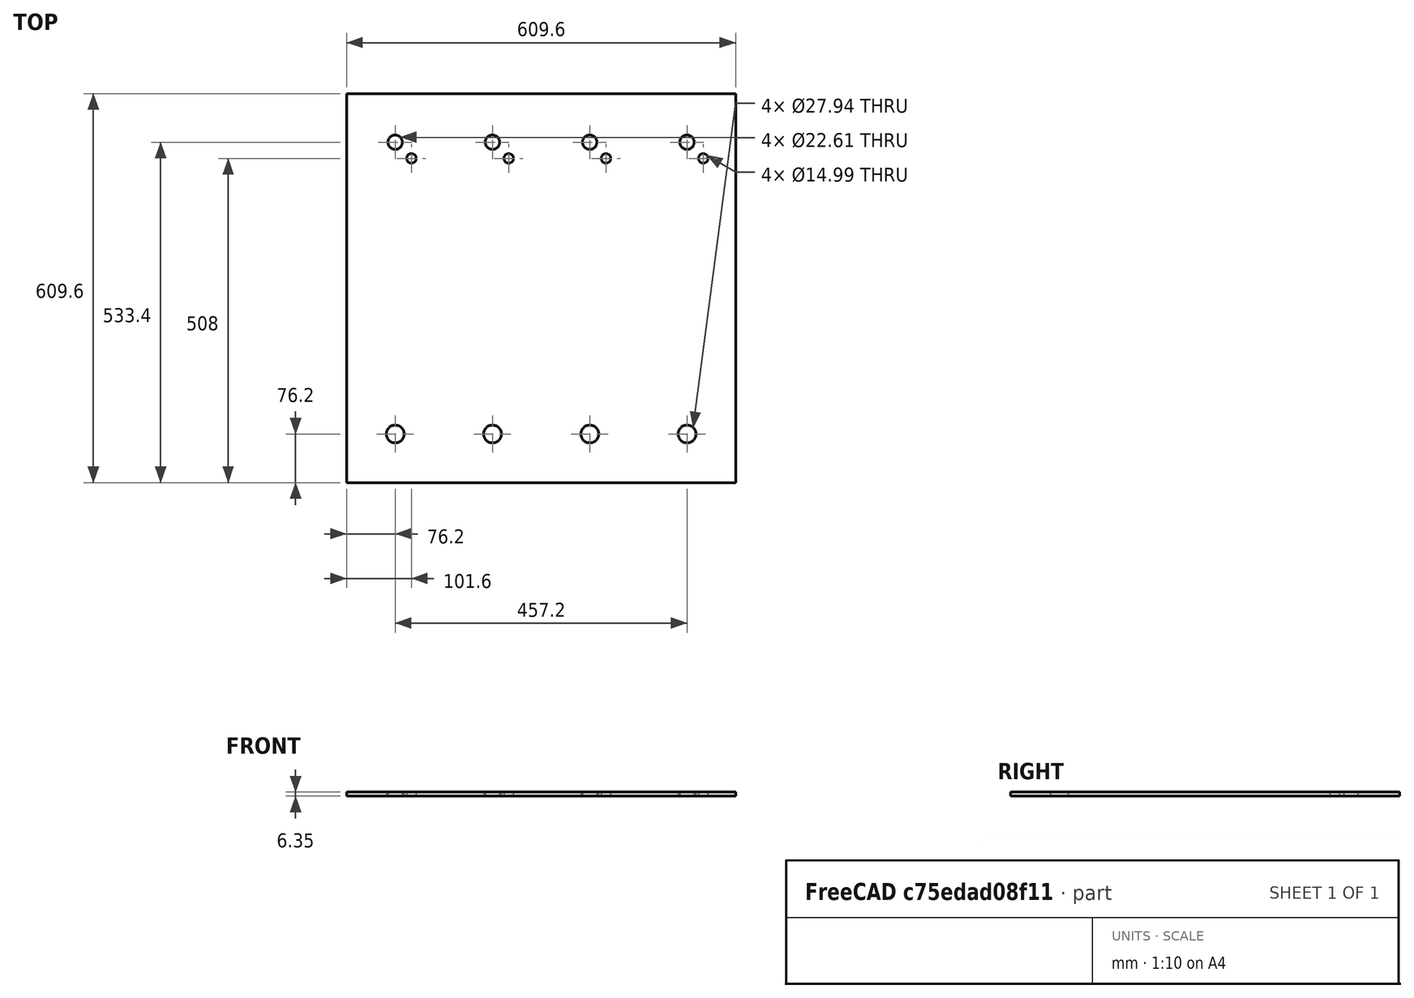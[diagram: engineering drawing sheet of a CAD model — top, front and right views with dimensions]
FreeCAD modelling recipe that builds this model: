
FCSTD DOCUMENT  (FreeCAD 0.16R6712 (Git))
Label: Frame Tank inner side
License: CreativeCommons Attribution
LicenseURL: http://creativecommons.org/licenses/by/4.0/
objects: Sketcher::SketchObject×1, PartDesign::Pad×1
note: 3 computed .brp shape members not serialized (recipe doc carries the construction recipe); baked Part::Feature solids carry a one-line shape summary decoded from their .brp

FEATURE [Sketcher::SketchObject] Sketch
  Placement = pos=(-304.8,-304.8,6.35) rot=(0,0,1;0rad)
  sketch-geometry (25):
    g0: Circle CenterX=-228.6 CenterY=228.6 CenterZ=0 NormalX=0 NormalY=0 NormalZ=1 Radius=11.303
    g1: Circle CenterX=-76.2 CenterY=228.6 CenterZ=0 NormalX=0 NormalY=0 NormalZ=1 Radius=11.303
    g2: Circle CenterX=76.2 CenterY=228.6 CenterZ=0 NormalX=0 NormalY=0 NormalZ=1 Radius=11.303
    g3: LineSegment [constr] StartX=-76.2 StartY=228.6 StartZ=0 EndX=76.2 EndY=228.6 EndZ=0
    g4: Circle CenterX=228.6 CenterY=228.6 CenterZ=0 NormalX=0 NormalY=0 NormalZ=1 Radius=11.303
    g5: LineSegment [constr] StartX=76.2 StartY=228.6 StartZ=0 EndX=228.6 EndY=228.6 EndZ=0
    g6: LineSegment [constr] StartX=-228.6 StartY=228.6 StartZ=0 EndX=-76.2 EndY=228.6 EndZ=0
    g7: LineSegment StartX=-304.8 StartY=304.8 StartZ=0 EndX=304.8 EndY=304.8 EndZ=0
    g8: LineSegment StartX=304.8 StartY=304.8 StartZ=0 EndX=304.8 EndY=-304.8 EndZ=0
    g9: LineSegment StartX=304.8 StartY=-304.8 StartZ=0 EndX=-304.8 EndY=-304.8 EndZ=0
    g10: LineSegment StartX=-304.8 StartY=-304.8 StartZ=0 EndX=-304.8 EndY=304.8 EndZ=0
    g11: Circle CenterX=-203.2 CenterY=203.2 CenterZ=0 NormalX=0 NormalY=0 NormalZ=1 Radius=7.493
    g12: Circle CenterX=-50.8 CenterY=203.2 CenterZ=0 NormalX=0 NormalY=0 NormalZ=1 Radius=7.493
    g13: LineSegment [constr] StartX=-203.2 StartY=203.2 StartZ=0 EndX=-50.8 EndY=203.2 EndZ=0
    g14: Circle CenterX=101.6 CenterY=203.2 CenterZ=0 NormalX=0 NormalY=0 NormalZ=1 Radius=7.493
    g15: LineSegment [constr] StartX=-50.8 StartY=203.2 StartZ=0 EndX=101.6 EndY=203.2 EndZ=0
    g16: Circle CenterX=254 CenterY=203.2 CenterZ=0 NormalX=0 NormalY=0 NormalZ=1 Radius=7.493
    g17: LineSegment [constr] StartX=101.6 StartY=203.2 StartZ=0 EndX=254 EndY=203.2 EndZ=0
    g18: Circle CenterX=-228.6 CenterY=-228.6 CenterZ=0 NormalX=0 NormalY=0 NormalZ=1 Radius=13.97
    g19: Circle CenterX=-76.2 CenterY=-228.6 CenterZ=0 NormalX=0 NormalY=0 NormalZ=1 Radius=13.97
    g20: LineSegment [constr] StartX=-228.6 StartY=-228.6 StartZ=0 EndX=-76.2 EndY=-228.6 EndZ=0
    g21: Circle CenterX=76.2 CenterY=-228.6 CenterZ=0 NormalX=0 NormalY=0 NormalZ=1 Radius=13.97
    g22: LineSegment [constr] StartX=-76.2 StartY=-228.6 StartZ=0 EndX=76.2 EndY=-228.6 EndZ=0
    g23: Circle CenterX=228.6 CenterY=-228.6 CenterZ=0 NormalX=0 NormalY=0 NormalZ=1 Radius=13.97
    g24: LineSegment [constr] StartX=76.2 StartY=-228.6 StartZ=0 EndX=228.6 EndY=-228.6 EndZ=0
  constraints (66):
    c: Radius(g0) = 11.303
    c: Equal(g0,g1) = 11.303
    c: Equal(g0,g2) = 11.303
    c: Coincident(g1,g3)
    c: Coincident(g2,g3)
    c: Equal(g0,g4) = 11.303
    c: Coincident(g2,g5)
    c: Coincident(g4,g5)
    c: Horizontal(g5)
    c: Horizontal(g3)
    c: Coincident(g6,g0)
    c: Coincident(g6,g1)
    c: Horizontal(g6)
    c: Equal(g5,g3)
    c: Equal(g3,g6)
    c: DistanceX(g6,g6) = 152.4
    c: Coincident(g7,g8)
    c: Coincident(g8,g9)
    c: Coincident(g9,g10)
    c: Coincident(g10,g7)
    c: Horizontal(g7)
    c: Horizontal(g9)
    c: Vertical(g8)
    c: Vertical(g10)
    c: Equal(g8,g9)
    c: DistanceY(g8,g8) = 609.6
    c: Symmetric(g8,g9,g-2)
    c: Symmetric(g8,g7,g-1)
    c: Symmetric(g0,g4,g-2)
    c: Radius(g11) = 7.493
    c: Equal(g11,g12) = 7.493
    c: Coincident(g11,g13)
    c: Coincident(g12,g13)
    c: Coincident(g12,g15)
    c: Coincident(g14,g15)
    c: Equal(g13,g15)
    c: Equal(g11,g16) = 7.493
    c: Coincident(g14,g17)
    c: Coincident(g16,g17)
    c: Equal(g13,g17)
    c: Horizontal(g13)
    c: Horizontal(g15)
    c: Horizontal(g17)
    c: Equal(g13,g6)
    c: DistanceX(g0,g11) = 25.4
    c: DistanceY(g11,g0) = 25.4
    c: Equal(g14,g12)
    c: Radius(g18) = 13.97
    c: Equal(g18,g19) = 13.97
    c: Coincident(g18,g20)
    c: Coincident(g19,g20)
    c: Distance(g20) = 152.4
    c: Equal(g18,g21) = 13.97
    c: Coincident(g19,g22)
    c: Coincident(g21,g22)
    c: Equal(g20,g22)
    c: Equal(g18,g23) = 13.97
    c: Coincident(g21,g24)
    c: Coincident(g23,g24)
    c: Equal(g20,g24)
    c: DistanceY(g9,g18) = 76.2
    c: Horizontal(g20)
    c: Horizontal(g22)
    c: Horizontal(g24)
    c: DistanceX(g9,g18) = 76.2
    c: DistanceY(g0,g7) = 76.2
FEATURE [PartDesign::Pad] Pad
  Length = 6.35
  Length2 = 100
  Placement = pos=(-304.8,-304.8,6.35) rot=(0,0,1;0rad)
  Sketch = -> Sketch
  Type = 0
